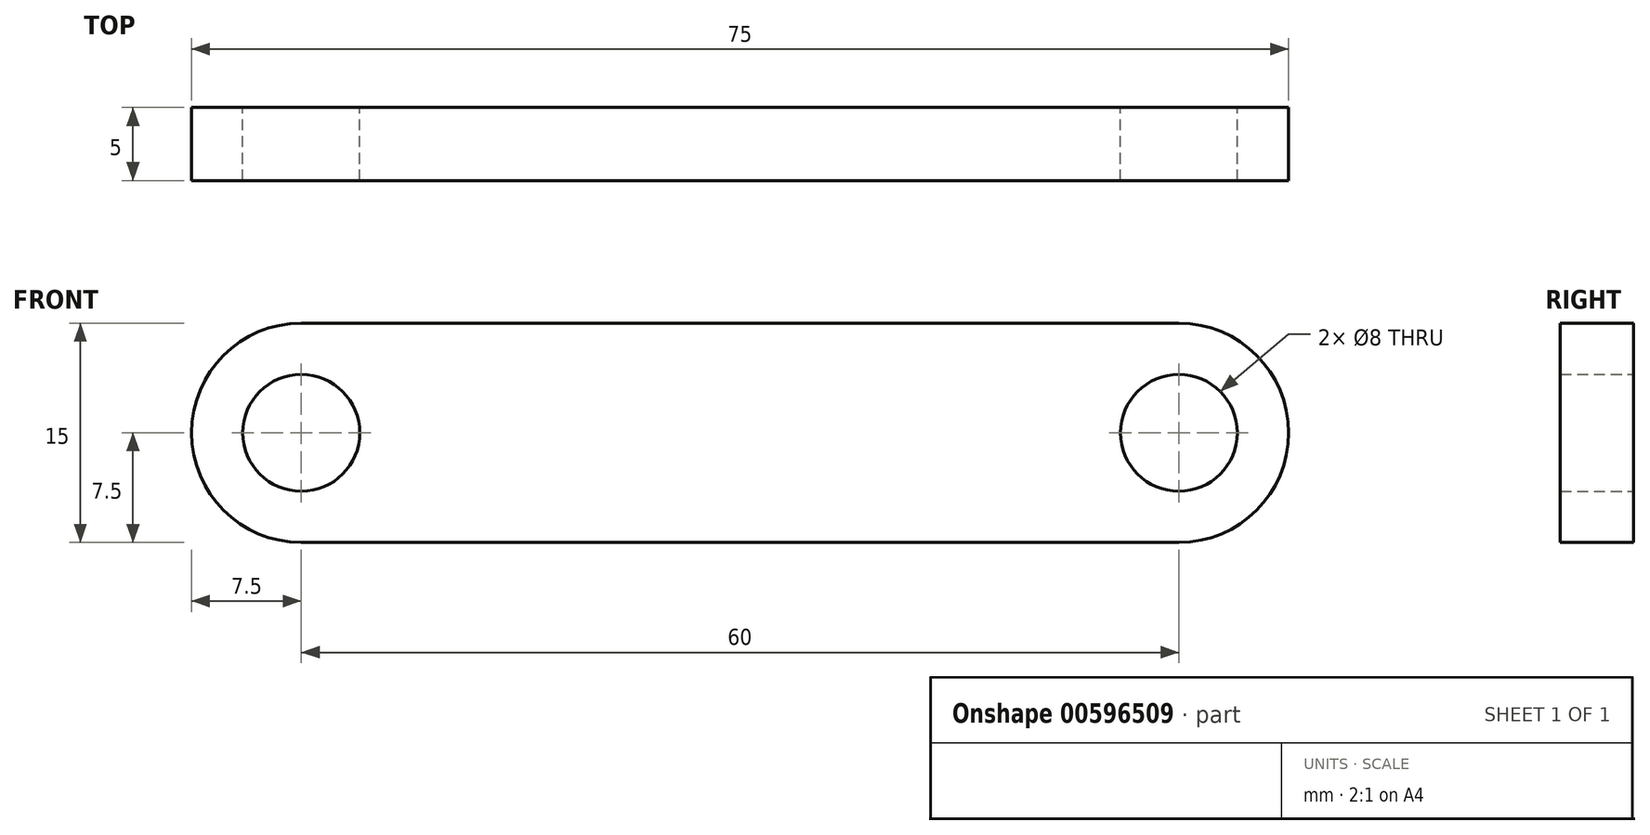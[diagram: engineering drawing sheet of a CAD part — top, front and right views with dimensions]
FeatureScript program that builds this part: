
annotation { "Feature Type Name" : "Feature", "Feature Type Description" : "" }
export const myFeature = defineFeature(function(context is Context, id is Id, definition is map)
    precondition{}
    {
        {
            var Q0;
            Q0=qCreatedBy(makeId("Front.planeOp"),FACE);
            var sketch = newSketch(context, id + "F0", { "sketchPlane" : qUnion([Q0])});
            skArc(sketch, "E0", {"start": v(0, 7.5) * mm, "mid": v(-7.5, 0) * mm, "end": v(0, -7.5) * mm});
            skCircle(sketch, "E1", {"center": v(0, 0) * mm, "radius": 4 * mm});
            skArc(sketch, "E2", {"start": v(60, -7.5) * mm, "mid": v(67.5, 0) * mm, "end": v(60, 7.5) * mm});
            skCircle(sketch, "E3", {"center": v(60, 0) * mm, "radius": 4 * mm});
            skLineSegment(sketch, "E4", {"start": v(0, 7.5) * mm, "end": v(60, 7.5) * mm});
            skLineSegment(sketch, "E5", {"start": v(0, -7.5) * mm, "end": v(60, -7.5) * mm});
            skSolve(sketch);
        }
        {
            var Q0;
            Q0 = qSketchRegion(id + "F0", true);
            extrude(context, id + "F1", {"entities" : qUnion([Q0]), "depth" : 5 * mm, "offsetDistance" : 25 * mm});
        }
    });
